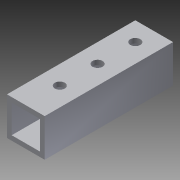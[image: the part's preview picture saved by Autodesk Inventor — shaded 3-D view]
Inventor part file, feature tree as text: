
AUTODESK INVENTOR PART (.ipt)
format: ipt  version: 2014 SP1 (Build 180222100, 222)  size: 103,424 bytes
history: native  units: in
note: dims shown in document units (in); Inventor stores cm internally (conversion verified against a paired STEP export)
features: extrude x2, sketch x2, pattern_linear x1
ambient origin geometry x8: Origin, YZ Plane, XZ Plane, XY Plane, X Axis, Y Axis, Z Axis, Center Point
bodies: Solid1 (feature_tree)
feature tree (5):
  extrude  "Extrusion1"  Depth=1.0in
  extrude  "Extrusion2"  Depth=3.4in TaperAngle=0.0deg
  pattern_linear  "Rectangular Pattern1"  Spacing1=0.5in  [1 undecoded]
  sketch  "Sketch1"  dims[d0=1.0in d1=1.0in]
  sketch  "Sketch2"  dims[d2=0.125in d3=3.4in d4=0.0in d5=0.5in d6=0.266in d7=3.4in d8=0.0in d9=1.1811in d11=1.0in]
note: 1 required parameter value undecoded (feature->parameter linkage not recoverable at this tier; creation-order binding heuristic only, values carry confidence <= 0.55)
